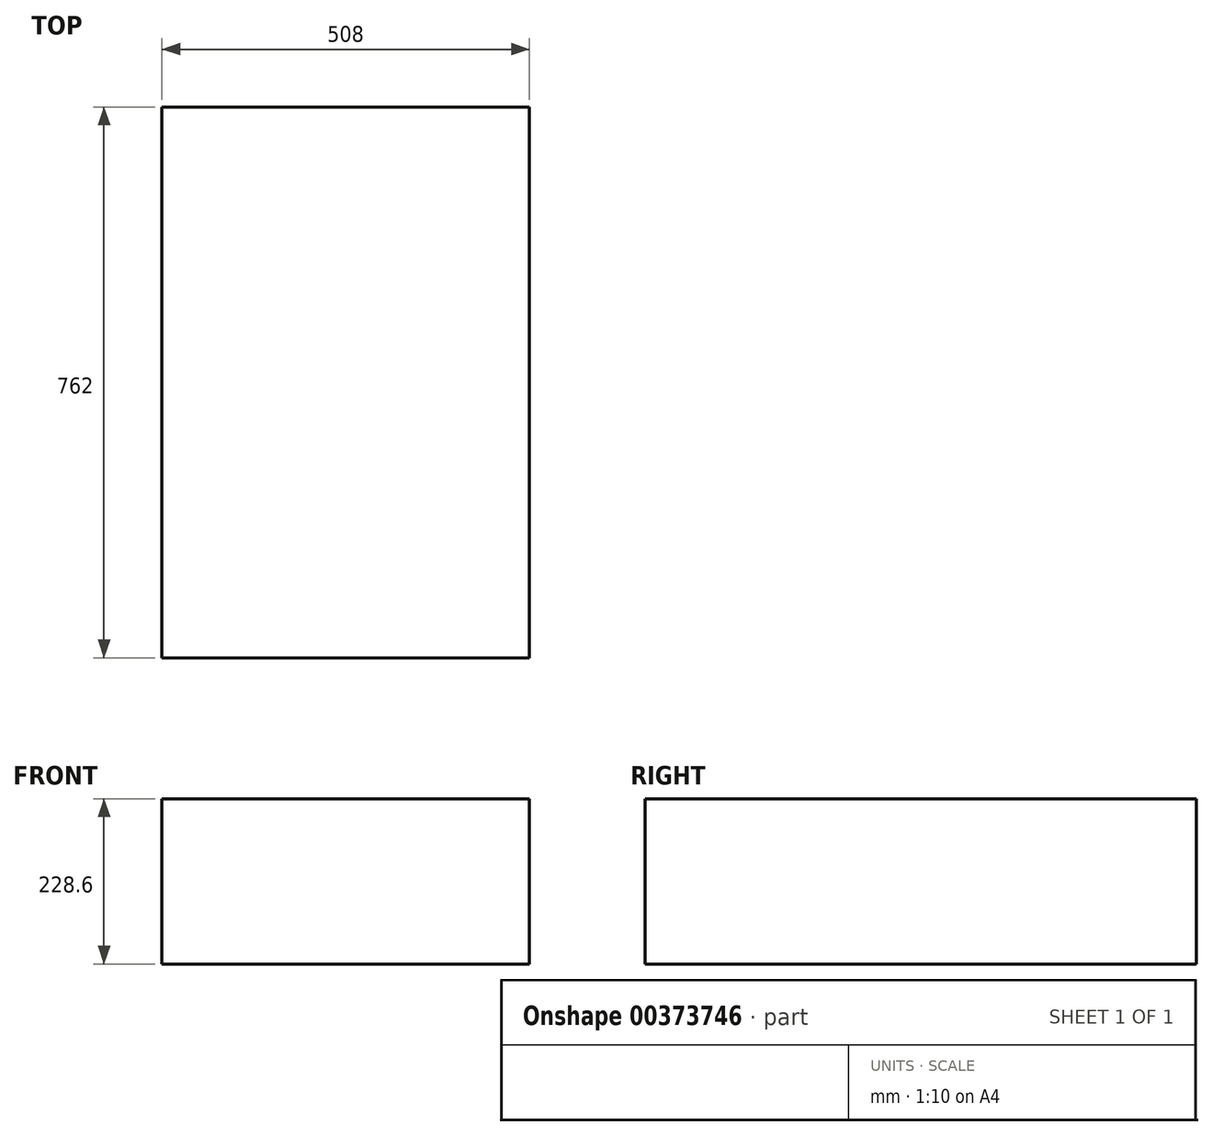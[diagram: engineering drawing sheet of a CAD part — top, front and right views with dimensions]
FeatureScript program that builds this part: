
annotation { "Feature Type Name" : "Feature", "Feature Type Description" : "" }
export const myFeature = defineFeature(function(context is Context, id is Id, definition is map)
    precondition{}
    {
        {
            var Q0;
            Q0=qCreatedBy(makeId("Top.planeOp"),FACE);
            var sketch = newSketch(context, id + "F0", { "sketchPlane" : qUnion([Q0])});
            skLineSegment(sketch, "E0.bottom", {"start": v(-286.72, 739.6) * mm, "end": v(221.28, 739.6) * mm});
            skLineSegment(sketch, "E0.top", {"start": v(-286.72, -22.4) * mm, "end": v(221.28, -22.4) * mm});
            skLineSegment(sketch, "E0.left", {"start": v(-286.72, 739.6) * mm, "end": v(-286.72, -22.4) * mm});
            skLineSegment(sketch, "E0.right", {"start": v(221.28, 739.6) * mm, "end": v(221.28, -22.4) * mm});
            skSolve(sketch);
        }
        {
            var Q0;
            Q0=makeQuery(id+"F0.imprint","IMPRINT",FACE,{"disambiguationData":[TD([[makeQuery(id+"F0.imprint","IMPRINT",EDGE,{"derivedFrom":sQuery(id+"F0.wireOp",EDGE,"E0.bottom")}),-1.0]])]});
            extrude(context, id + "F1", {"entities" : qUnion([Q0]), "depth" : 228.6 * mm});
        }
    });
